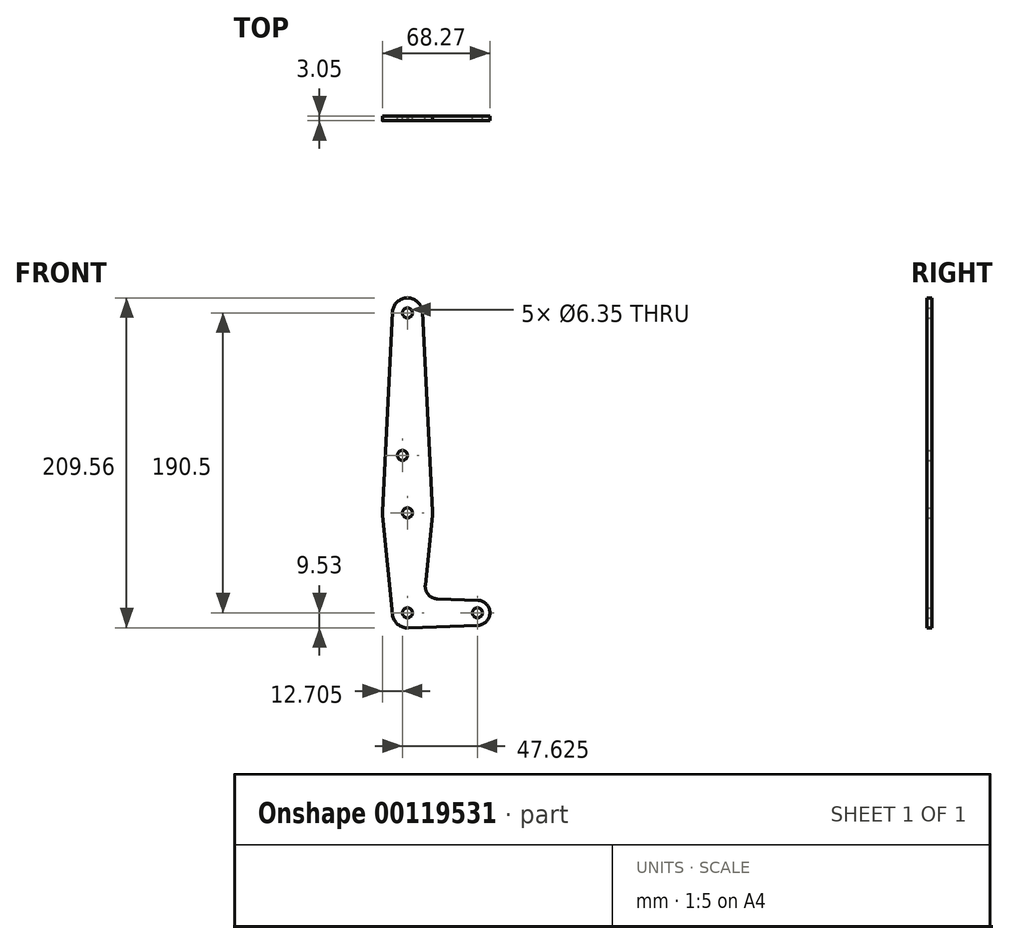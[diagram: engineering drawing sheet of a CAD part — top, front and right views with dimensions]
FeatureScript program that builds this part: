
annotation { "Feature Type Name" : "Feature", "Feature Type Description" : "" }
export const myFeature = defineFeature(function(context is Context, id is Id, definition is map)
    precondition{}
    {
        {
            var Q0;
            Q0=qCreatedBy(makeId("Front.planeOp"),FACE);
            var sketch = newSketch(context, id + "F0", { "sketchPlane" : qUnion([Q0])});
            skCircle(sketch, "E0", {"center": v(0, 0) * mm, "radius": 9.53 * mm});
            skCircle(sketch, "E1", {"center": v(44.45, 0) * mm, "radius": 7.94 * mm});
            skCircle(sketch, "E2", {"center": v(0, 190.5) * mm, "radius": 9.53 * mm});
            skCircle(sketch, "E3", {"center": v(0, 63.5) * mm, "radius": 15.88 * mm});
            skLineSegment(sketch, "E4", {"start": v(0, 190.5) * mm, "end": v(0, 0) * mm, "construction": true});
            skLineSegment(sketch, "E5", {"start": v(0, 0) * mm, "end": v(44.45, 0) * mm, "construction": true});
            skLineSegment(sketch, "E6", {"start": v(-9.51, 190.98) * mm, "end": v(-15.86, 64.3) * mm});
            skLineSegment(sketch, "E7", {"start": v(9.51, 190.98) * mm, "end": v(15.86, 64.3) * mm});
            skLineSegment(sketch, "E8", {"start": v(-15.8, 61.91) * mm, "end": v(-9.48, -0.95) * mm});
            skLineSegment(sketch, "E9", {"start": v(15.8, 61.91) * mm, "end": v(11.34, 17.6) * mm});
            skCircle(sketch, "E10", {"center": v(0, 190.5) * mm, "radius": 3.18 * mm});
            skCircle(sketch, "E11", {"center": v(-3.17, 100.03) * mm, "radius": 3.18 * mm});
            skCircle(sketch, "E12", {"center": v(0, 63.5) * mm, "radius": 3.18 * mm});
            skCircle(sketch, "E13", {"center": v(0, 0) * mm, "radius": 3.18 * mm});
            skCircle(sketch, "E14", {"center": v(44.45, 0) * mm, "radius": 3.18 * mm});
            skLineSegment(sketch, "E15", {"start": v(18.97, 8.85) * mm, "end": v(44.73, 7.93) * mm});
            skLineSegment(sketch, "E16", {"start": v(0, -9.53) * mm, "end": v(44.73, -7.93) * mm});
            skArc(sketch, "E17.filletArc", {"start": v(11.34, 17.6) * mm, "mid": v(13.26, 11.57) * mm, "end": v(18.97, 8.85) * mm});
            skSolve(sketch);
        }
        {
            var Q0;
            Q0 = qSketchRegion(id + "F0", true);
            extrude(context, id + "F1", {"entities" : qUnion([Q0]), "depth" : 3.05 * mm});
        }
    });
